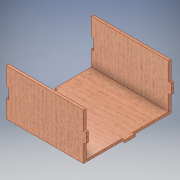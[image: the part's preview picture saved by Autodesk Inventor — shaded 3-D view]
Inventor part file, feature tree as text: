
AUTODESK INVENTOR PART (.ipt)
format: ipt  version: 2017 (Build 210142000, 142)  size: 228,352 bytes
history: native  units: in
note: dims shown in document units (in); Inventor stores cm internally (conversion verified against a paired STEP export)
features: extrude x6, sketch x6, fillet x2, hole x2
ambient origin geometry x8: Origin, YZ Plane, XZ Plane, XY Plane, X Axis, Y Axis, Z Axis, Center Point
bodies: Solid1 (feature_tree)
feature tree (16):
  extrude  "Extrusion1"  Depth=2.9528in
  extrude  "Extrusion2"  Depth=2.9528in
  extrude  "Extrusion3"  Depth=5.9055in
  extrude  "Extrusion4"  Depth=0.1875in TaperAngle=0.0deg
  extrude  "Extrusion5"  Depth=0.1875in
  extrude  "Extrusion6"  Depth=0.7874in
  fillet  "Fillet1"  Radius=0.1969in
  fillet  "Fillet2"  Radius=1.378in
  hole  "Hole1"  [1 undecoded]
  hole  "Hole2"  [1 undecoded]
  sketch  "Sketch1"  dims[d0=5.9055in d1=6.6929in d2=0.1969in d3=0.1969in d4=2.9528in d5=2.9528in d6=0.7874in d9=0.0in d10=2.9528in]
  sketch  "Sketch2"  dims[d11=0.1969in d12=2.9528in]
  sketch  "Sketch3"  dims[d13=0.7874in d14=5.9055in]
  sketch  "Sketch4"  dims[d15=0.0in d16=0.1875in d17=0.0in]
  sketch  "Sketch5"  dims[d18=0.1875in d19=0.1875in]
  sketch  "Sketch6"  dims[d20=3.3558in d21=0.0in d22=0.7874in d23=0.1969in d24=1.378in d25=1.378in d26=0.1875in d27=0.0in d28=0.7874in d29=0.1969in d30=1.378in d31=1.378in d32=0.1875in d33=0.0in d34=0.7874in d35=0.1969in d36=1.378in d37=1.378in d38=0.1875in d39=0.0in d40=0.1875in d41=0.0in d42=0.0394in d43=0.0394in d44=1.0in d45=1.0in d46=0.0984in d47=0.75in d48=0.375in d49=0.25in d50=0.5635in d51=0.1969in d52=0.8108in d53=1.0in d54=1.0in d55=0.0984in d56=0.75in d57=0.375in d58=0.25in d59=0.5635in d60=0.1969in d61=0.8108in]
note: 2 required parameter values undecoded (feature->parameter linkage not recoverable at this tier; creation-order binding heuristic only, values carry confidence <= 0.55)
